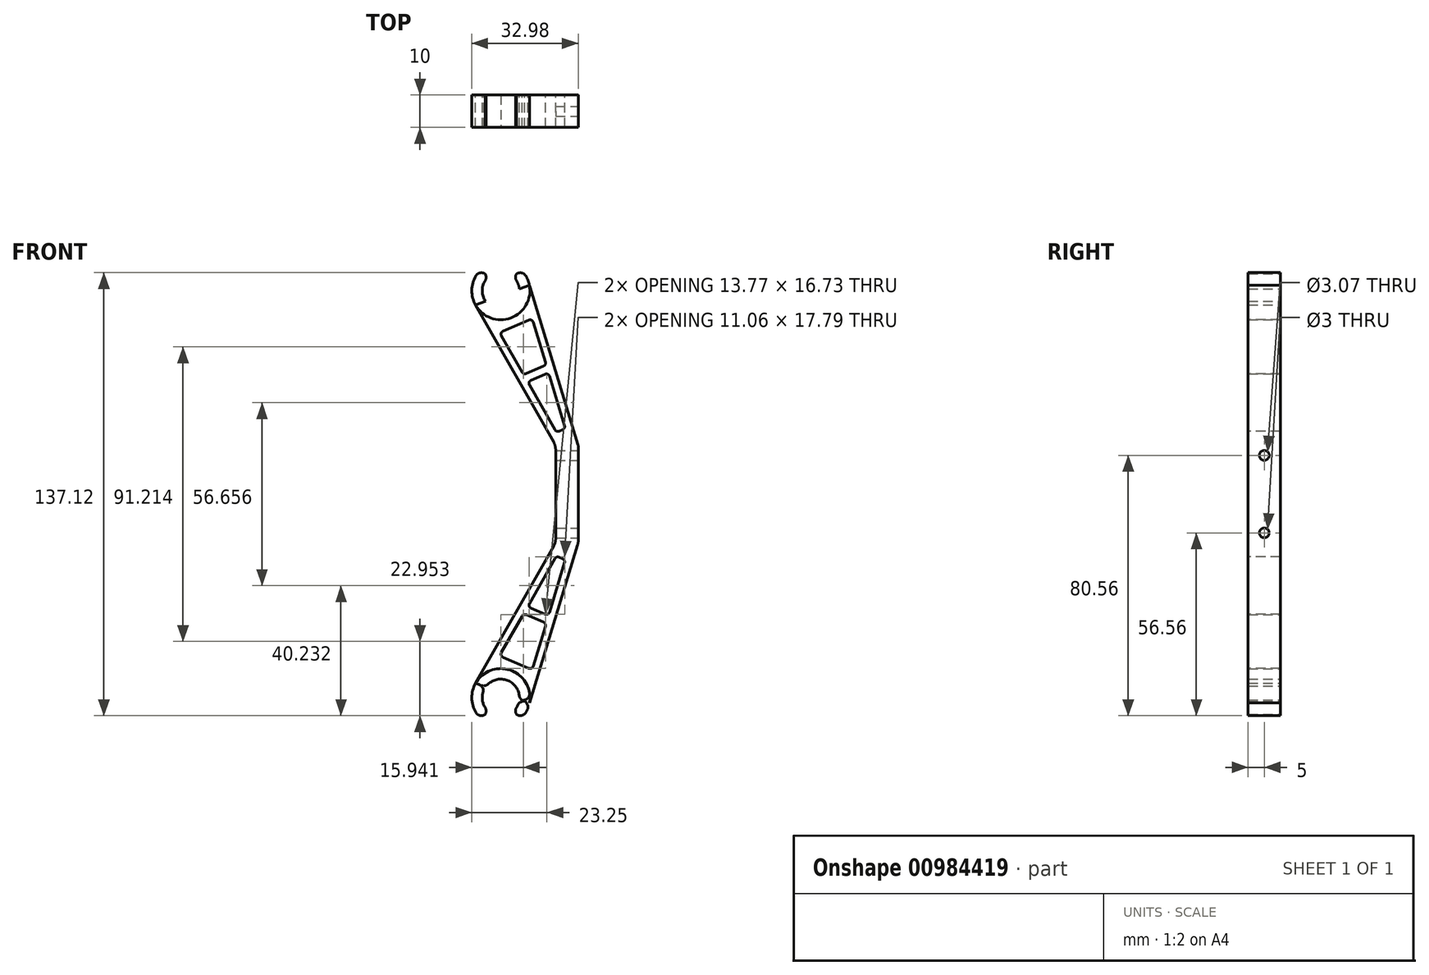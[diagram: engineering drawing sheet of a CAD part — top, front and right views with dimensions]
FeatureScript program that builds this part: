
annotation { "Feature Type Name" : "Feature", "Feature Type Description" : "" }
export const myFeature = defineFeature(function(context is Context, id is Id, definition is map)
    precondition{}
    {
        {
            var Q0;
            Q0=qCreatedBy(makeId("Front.planeOp"),FACE);
            var sketch = newSketch(context, id + "F0", { "sketchPlane" : qUnion([Q0])});
            skPoint(sketch, "E0.middle", {"position": v(16, 0) * mm});
            skCircle(sketch, "E1", {"center": v(-4.47, -63) * mm, "radius": 5.75 * mm});
            skCircle(sketch, "E2", {"center": v(-4.47, -63) * mm, "radius": 9 * mm});
            skLineSegment(sketch, "E3", {"start": v(12.5, -15) * mm, "end": v(-12.3, -58.55) * mm});
            skLineSegment(sketch, "E4", {"start": v(19.5, -15) * mm, "end": v(4.43, -64.65) * mm});
            skLineSegment(sketch, "E5", {"start": v(5.21, -54.33) * mm, "end": v(9.57, -39.98) * mm});
            skLineSegment(sketch, "E6", {"start": v(2.58, -36.97) * mm, "end": v(-4.84, -50) * mm});
            skLineSegment(sketch, "E7", {"start": v(-4.84, -50) * mm, "end": v(5.21, -54.33) * mm});
            skLineSegment(sketch, "E8", {"start": v(2.58, -36.97) * mm, "end": v(9.57, -39.98) * mm});
            skLineSegment(sketch, "E9", {"start": v(3.82, -34.8) * mm, "end": v(12.73, -19.16) * mm});
            skLineSegment(sketch, "E10", {"start": v(10.3, -37.59) * mm, "end": v(15.53, -20.36) * mm});
            skLineSegment(sketch, "E11", {"start": v(3.82, -34.8) * mm, "end": v(10.3, -37.59) * mm});
            skLineSegment(sketch, "E12", {"start": v(12.73, -19.16) * mm, "end": v(15.53, -20.36) * mm});
            skLineSegment(sketch, "E13.MirrorCS", {"start": v(12.73, 19.16) * mm, "end": v(15.53, 20.36) * mm});
            skLineSegment(sketch, "E14.MirrorCS", {"start": v(-4.84, 50) * mm, "end": v(5.21, 54.33) * mm});
            skLineSegment(sketch, "E15.MirrorCS", {"start": v(12.5, 15) * mm, "end": v(-12.3, 58.55) * mm});
            skLineSegment(sketch, "E16.MirrorCS", {"start": v(10.3, 37.59) * mm, "end": v(15.53, 20.36) * mm});
            skLineSegment(sketch, "E17.MirrorCS", {"start": v(3.82, 34.8) * mm, "end": v(12.73, 19.16) * mm});
            skLineSegment(sketch, "E18.MirrorCS", {"start": v(2.58, 36.97) * mm, "end": v(-4.84, 50) * mm});
            skLineSegment(sketch, "E19.MirrorCS", {"start": v(3.82, 34.8) * mm, "end": v(10.3, 37.59) * mm});
            skLineSegment(sketch, "E20.MirrorCS", {"start": v(19.5, 15) * mm, "end": v(4.43, 64.65) * mm});
            skLineSegment(sketch, "E21.MirrorCS", {"start": v(5.21, 54.33) * mm, "end": v(9.57, 39.98) * mm});
            skLineSegment(sketch, "E22.MirrorCS", {"start": v(2.58, 36.97) * mm, "end": v(9.57, 39.98) * mm});
            skLineSegment(sketch, "E23", {"start": v(12.5, -15) * mm, "end": v(12.5, 15) * mm});
            skLineSegment(sketch, "E24", {"start": v(19.5, 15) * mm, "end": v(19.5, -15) * mm});
            skLineSegment(sketch, "E25", {"start": v(-12.3, 58.55) * mm, "end": v(4.43, 64.65) * mm});
            skLineSegment(sketch, "E26", {"start": v(-12.3, -58.55) * mm, "end": v(4.43, -64.65) * mm});
            skLineSegment(sketch, "E27", {"start": v(-10.6, -69.6) * mm, "end": v(-8.38, -67.22) * mm});
            skLineSegment(sketch, "E28", {"start": v(1.65, -69.6) * mm, "end": v(-0.56, -67.22) * mm});
            skCircle(sketch, "E29.MirrorC", {"center": v(-4.47, 63) * mm, "radius": 9 * mm});
            skLineSegment(sketch, "E30.MirrorCS", {"start": v(1.65, 69.6) * mm, "end": v(-0.56, 67.22) * mm});
            skLineSegment(sketch, "E31.MirrorCS", {"start": v(-10.6, 69.6) * mm, "end": v(-8.38, 67.22) * mm});
            skCircle(sketch, "E32.MirrorC", {"center": v(-4.47, 63) * mm, "radius": 5.75 * mm});
            skSolve(sketch);
        }
        {
            var Q0;
            {var subQ6=sQuery(id+"F0.wireOp",EDGE,"E3");Q0=makeQuery(id+"F0.imprint","IMPRINT",FACE,{"disambiguationData":[TD([[makeQuery(id+"F0.imprint","IMPRINT",EDGE,{"derivedFrom":subQ6}),1.0]])]});}
            var Q1;
            {var subQ0=sQuery(id+"F0.wireOp",EDGE,"E26");var subQ1=sQuery(id+"F0.wireOp",EDGE,"E1");var subQ2=makeQuery(id+"F0.imprint","INTERSECT",VERTEX,{"disambiguationData":[OD(0.0)],"derivedFrom":[subQ1,subQ0]});Q1=makeQuery(id+"F0.imprint","IMPRINT",FACE,{"disambiguationData":[TD([[makeQuery(id+"F0.imprint","IMPRINT",EDGE,{"disambiguationData":[TD([[subQ2,1.0]])],"derivedFrom":subQ1}),-1.0]])]});}
            var Q2;
            {var subQ0=sQuery(id+"F0.wireOp",EDGE,"XQdszwVE-5wpe-kycQ-sRSQ-Fq0FjsTCC5aD");Q2=makeQuery(id+"F0.imprint","IMPRINT",FACE,{"disambiguationData":[TD([[makeQuery(id+"F0.imprint","IMPRINT",EDGE,{"derivedFrom":subQ0}),1.0]])]});}
            var Q3;
            {var subQ0=sQuery(id+"F0.wireOp",EDGE,"Yc0Pc47L-QJd6-gHrf-0qyo-1opZ7JtCYNZG");Q3=makeQuery(id+"F0.imprint","IMPRINT",FACE,{"disambiguationData":[TD([[makeQuery(id+"F0.imprint","IMPRINT",EDGE,{"derivedFrom":subQ0}),-1.0]])]});}
            var Q4;
            {var subQ0=sQuery(id+"F0.wireOp",EDGE,"E25");var subQ4=sQuery(id+"F0.wireOp",EDGE,"E143.MirrorC");var subQ5=makeQuery(id+"F0.imprint","INTERSECT",VERTEX,{"disambiguationData":[OD(0.0)],"derivedFrom":[subQ4,subQ0]});Q4=makeQuery(id+"F0.imprint","IMPRINT",FACE,{"disambiguationData":[TD([[makeQuery(id+"F0.imprint","IMPRINT",EDGE,{"disambiguationData":[TD([[subQ5,1.0]])],"derivedFrom":subQ4}),1.0]])]});}
            var Q5;
            {var subQ0=sQuery(id+"F0.wireOp",EDGE,"b6da1f22-f3a6-460e-9121-5a5fd05a2c0d7.MirrorCS");Q5=makeQuery(id+"F0.imprint","IMPRINT",FACE,{"disambiguationData":[TD([[makeQuery(id+"F0.imprint","IMPRINT",EDGE,{"derivedFrom":subQ0}),1.0]])]});}
            var Q6;
            {var subQ3=sQuery(id+"F0.wireOp",EDGE,"E141.MirrorCS");Q6=makeQuery(id+"F0.imprint","IMPRINT",FACE,{"disambiguationData":[TD([[makeQuery(id+"F0.imprint","IMPRINT",EDGE,{"derivedFrom":subQ3}),-1.0]])]});}
            var Q7;
            {var subQ0=sQuery(id+"F0.wireOp",EDGE,"E27");Q7=makeQuery(id+"F0.imprint","IMPRINT",FACE,{"disambiguationData":[TD([[makeQuery(id+"F0.imprint","IMPRINT",EDGE,{"derivedFrom":subQ0}),1.0]])]});}
            var Q8;
            {var subQ0=sQuery(id+"F0.wireOp",EDGE,"E28");Q8=makeQuery(id+"F0.imprint","IMPRINT",FACE,{"disambiguationData":[TD([[makeQuery(id+"F0.imprint","IMPRINT",EDGE,{"derivedFrom":subQ0}),-1.0]])]});}
            var Q9;
            {var subQ0=sQuery(id+"F0.wireOp",EDGE,"E25");var subQ1=sQuery(id+"F0.wireOp",EDGE,"E29.MirrorC");var subQ3=makeQuery(id+"F0.imprint","INTERSECT",VERTEX,{"derivedFrom":[subQ1,subQ0]});Q9=makeQuery(id+"F0.imprint","IMPRINT",FACE,{"disambiguationData":[TD([[makeQuery(id+"F0.imprint","IMPRINT",EDGE,{"disambiguationData":[TD([[subQ3,1.0]])],"derivedFrom":subQ0}),-1.0]])]});}
            var Q10;
            {var subQ3=sQuery(id+"F0.wireOp",EDGE,"E31.MirrorCS");Q10=makeQuery(id+"F0.imprint","IMPRINT",FACE,{"disambiguationData":[TD([[makeQuery(id+"F0.imprint","IMPRINT",EDGE,{"derivedFrom":subQ3}),-1.0]])]});}
            var Q11;
            {var subQ0=sQuery(id+"F0.wireOp",EDGE,"E30.MirrorCS");Q11=makeQuery(id+"F0.imprint","IMPRINT",FACE,{"disambiguationData":[TD([[makeQuery(id+"F0.imprint","IMPRINT",EDGE,{"derivedFrom":subQ0}),1.0]])]});}
            extrude(context, id + "F1", {"entities" : qUnion([Q0, Q1, Q2, Q3, Q4, Q5, Q6, Q7, Q8, Q9, Q10, Q11]), "depth" : 10 * mm, "offsetDistance" : 25 * mm});
        }
        {
            var Q0;
            Q0=makeQuery(id+"F1.opExtrude","SWEPT_EDGE",EDGE,{"disambiguationData":[OSD([sQuery(id+"F0.wireOp",EDGE,"E10"),sQuery(id+"F0.wireOp",EDGE,"E12")])]});
            var Q1;
            Q1=makeQuery(id+"F1.opExtrude","SWEPT_EDGE",EDGE,{"disambiguationData":[OSD([sQuery(id+"F0.wireOp",EDGE,"E9"),sQuery(id+"F0.wireOp",EDGE,"E12")])]});
            var Q2;
            Q2=makeQuery(id+"F1.opExtrude","SWEPT_EDGE",EDGE,{"disambiguationData":[OSD([sQuery(id+"F0.wireOp",EDGE,"E9"),sQuery(id+"F0.wireOp",EDGE,"E11")])]});
            var Q3;
            Q3=makeQuery(id+"F1.opExtrude","SWEPT_EDGE",EDGE,{"disambiguationData":[OSD([sQuery(id+"F0.wireOp",EDGE,"E10"),sQuery(id+"F0.wireOp",EDGE,"E11")])]});
            var Q4;
            Q4=makeQuery(id+"F1.opExtrude","SWEPT_EDGE",EDGE,{"disambiguationData":[OSD([sQuery(id+"F0.wireOp",EDGE,"E5"),sQuery(id+"F0.wireOp",EDGE,"E8")])]});
            var Q5;
            Q5=makeQuery(id+"F1.opExtrude","SWEPT_EDGE",EDGE,{"disambiguationData":[OSD([sQuery(id+"F0.wireOp",EDGE,"E6"),sQuery(id+"F0.wireOp",EDGE,"E8")])]});
            var Q6;
            Q6=makeQuery(id+"F1.opExtrude","SWEPT_EDGE",EDGE,{"disambiguationData":[OSD([sQuery(id+"F0.wireOp",EDGE,"E5"),sQuery(id+"F0.wireOp",EDGE,"E7")])]});
            var Q7;
            Q7=makeQuery(id+"F1.opExtrude","SWEPT_EDGE",EDGE,{"disambiguationData":[OSD([sQuery(id+"F0.wireOp",EDGE,"E6"),sQuery(id+"F0.wireOp",EDGE,"E7")])]});
            var Q8;
            Q8=makeQuery(id+"F1.opExtrude","SWEPT_EDGE",EDGE,{"disambiguationData":[OSD([sQuery(id+"F0.wireOp",EDGE,"E13.MirrorCS"),sQuery(id+"F0.wireOp",EDGE,"E16.MirrorCS")])]});
            var Q9;
            Q9=makeQuery(id+"F1.opExtrude","SWEPT_EDGE",EDGE,{"disambiguationData":[OSD([sQuery(id+"F0.wireOp",EDGE,"E13.MirrorCS"),sQuery(id+"F0.wireOp",EDGE,"E17.MirrorCS")])]});
            var Q10;
            Q10=makeQuery(id+"F1.opExtrude","SWEPT_EDGE",EDGE,{"disambiguationData":[OSD([sQuery(id+"F0.wireOp",EDGE,"E17.MirrorCS"),sQuery(id+"F0.wireOp",EDGE,"E19.MirrorCS")])]});
            var Q11;
            Q11=makeQuery(id+"F1.opExtrude","SWEPT_EDGE",EDGE,{"disambiguationData":[OSD([sQuery(id+"F0.wireOp",EDGE,"E16.MirrorCS"),sQuery(id+"F0.wireOp",EDGE,"E19.MirrorCS")])]});
            var Q12;
            Q12=makeQuery(id+"F1.opExtrude","SWEPT_EDGE",EDGE,{"disambiguationData":[OSD([sQuery(id+"F0.wireOp",EDGE,"E14.MirrorCS"),sQuery(id+"F0.wireOp",EDGE,"E21.MirrorCS")])]});
            var Q13;
            Q13=makeQuery(id+"F1.opExtrude","SWEPT_EDGE",EDGE,{"disambiguationData":[OSD([sQuery(id+"F0.wireOp",EDGE,"E14.MirrorCS"),sQuery(id+"F0.wireOp",EDGE,"E18.MirrorCS")])]});
            var Q14;
            Q14=makeQuery(id+"F1.opExtrude","SWEPT_EDGE",EDGE,{"disambiguationData":[OSD([sQuery(id+"F0.wireOp",EDGE,"E18.MirrorCS"),sQuery(id+"F0.wireOp",EDGE,"E22.MirrorCS")])]});
            var Q15;
            Q15=makeQuery(id+"F1.opExtrude","SWEPT_EDGE",EDGE,{"disambiguationData":[OSD([sQuery(id+"F0.wireOp",EDGE,"E21.MirrorCS"),sQuery(id+"F0.wireOp",EDGE,"E22.MirrorCS")])]});
            fillet(context, id + "F2", {"entities" : qUnion([Q0, Q1, Q2, Q3, Q4, Q5, Q6, Q7, Q8, Q9, Q10, Q11, Q12, Q13, Q14, Q15]), "radius" : 1 * mm, "tangentPropagation" : true, "allowEdgeOverflow" : false});
        }
        {
            var Q0;
            Q0=makeQuery(id+"F1.opExtrude","SWEPT_EDGE",EDGE,{"disambiguationData":[OSD([sQuery(id+"F0.wireOp",EDGE,"b6da1f22-f3a6-460e-9121-5a5fd05a2c0d4.MirrorC"),sQuery(id+"F0.wireOp",EDGE,"E141.MirrorCS")])]});
            var Q1;
            Q1=makeQuery(id+"F1.opExtrude","SWEPT_EDGE",EDGE,{"disambiguationData":[OSD([sQuery(id+"F0.wireOp",EDGE,"E141.MirrorCS"),sQuery(id+"F0.wireOp",EDGE,"E143.MirrorC")])]});
            var Q2;
            Q2=makeQuery(id+"F1.opExtrude","SWEPT_EDGE",EDGE,{"disambiguationData":[OSD([sQuery(id+"F0.wireOp",EDGE,"b6da1f22-f3a6-460e-9121-5a5fd05a2c0d7.MirrorCS"),sQuery(id+"F0.wireOp",EDGE,"E143.MirrorC")])]});
            var Q3;
            Q3=makeQuery(id+"F1.opExtrude","SWEPT_EDGE",EDGE,{"disambiguationData":[OSD([sQuery(id+"F0.wireOp",EDGE,"b6da1f22-f3a6-460e-9121-5a5fd05a2c0d4.MirrorC"),sQuery(id+"F0.wireOp",EDGE,"b6da1f22-f3a6-460e-9121-5a5fd05a2c0d7.MirrorCS")])]});
            var Q4;
            Q4=makeQuery(id+"F1.opExtrude","SWEPT_EDGE",EDGE,{"disambiguationData":[OSD([sQuery(id+"F0.wireOp",EDGE,"E2"),sQuery(id+"F0.wireOp",EDGE,"Yc0Pc47L-QJd6-gHrf-0qyo-1opZ7JtCYNZG")])]});
            var Q5;
            Q5=makeQuery(id+"F1.opExtrude","SWEPT_EDGE",EDGE,{"disambiguationData":[OSD([sQuery(id+"F0.wireOp",EDGE,"E1"),sQuery(id+"F0.wireOp",EDGE,"Yc0Pc47L-QJd6-gHrf-0qyo-1opZ7JtCYNZG")])]});
            var Q6;
            Q6=makeQuery(id+"F1.opExtrude","SWEPT_EDGE",EDGE,{"disambiguationData":[OSD([sQuery(id+"F0.wireOp",EDGE,"E1"),sQuery(id+"F0.wireOp",EDGE,"XQdszwVE-5wpe-kycQ-sRSQ-Fq0FjsTCC5aD")])]});
            var Q7;
            Q7=makeQuery(id+"F1.opExtrude","SWEPT_EDGE",EDGE,{"disambiguationData":[OSD([sQuery(id+"F0.wireOp",EDGE,"E2"),sQuery(id+"F0.wireOp",EDGE,"XQdszwVE-5wpe-kycQ-sRSQ-Fq0FjsTCC5aD")])]});
            var Q8;
            Q8=makeQuery(id+"F1.opExtrude","SWEPT_EDGE",EDGE,{"disambiguationData":[OSD([sQuery(id+"F0.wireOp",EDGE,"E20.MirrorCS"),sQuery(id+"F0.wireOp",EDGE,"E25")])]});
            var Q9;
            Q9=makeQuery(id+"F1.opExtrude","SWEPT_EDGE",EDGE,{"disambiguationData":[OSD([sQuery(id+"F0.wireOp",EDGE,"E29.MirrorC"),sQuery(id+"F0.wireOp",EDGE,"E30.MirrorCS")])]});
            var Q10;
            Q10=makeQuery(id+"F1.opExtrude","SWEPT_EDGE",EDGE,{"disambiguationData":[OSD([sQuery(id+"F0.wireOp",EDGE,"E30.MirrorCS"),sQuery(id+"F0.wireOp",EDGE,"E32.MirrorC")])]});
            var Q11;
            Q11=makeQuery(id+"F1.opExtrude","SWEPT_EDGE",EDGE,{"disambiguationData":[OSD([sQuery(id+"F0.wireOp",EDGE,"E31.MirrorCS"),sQuery(id+"F0.wireOp",EDGE,"E32.MirrorC")])]});
            var Q12;
            Q12=makeQuery(id+"F1.opExtrude","SWEPT_EDGE",EDGE,{"disambiguationData":[OSD([sQuery(id+"F0.wireOp",EDGE,"E29.MirrorC"),sQuery(id+"F0.wireOp",EDGE,"E31.MirrorCS")])]});
            fillet(context, id + "F3", {"entities" : qUnion([Q0, Q1, Q2, Q3, Q4, Q5, Q6, Q7, Q8, Q9, Q10, Q11, Q12]), "radius" : 2 * mm, "tangentPropagation" : true, "allowEdgeOverflow" : false});
        }
        {
            var Q0;
            Q0=makeQuery(id+"F1.opExtrude","SWEPT_EDGE",EDGE,{"disambiguationData":[OSD([sQuery(id+"F0.wireOp",EDGE,"E3"),sQuery(id+"F0.wireOp",EDGE,"E23")])]});
            var Q1;
            Q1=makeQuery(id+"F1.opExtrude","SWEPT_EDGE",EDGE,{"disambiguationData":[OSD([sQuery(id+"F0.wireOp",EDGE,"E15.MirrorCS"),sQuery(id+"F0.wireOp",EDGE,"E23")])]});
            var Q2;
            Q2=makeQuery(id+"F1.opExtrude","SWEPT_EDGE",EDGE,{"disambiguationData":[OSD([sQuery(id+"F0.wireOp",EDGE,"E4"),sQuery(id+"F0.wireOp",EDGE,"E24")])]});
            var Q3;
            Q3=makeQuery(id+"F1.opExtrude","SWEPT_EDGE",EDGE,{"disambiguationData":[OSD([sQuery(id+"F0.wireOp",EDGE,"E20.MirrorCS"),sQuery(id+"F0.wireOp",EDGE,"E24")])]});
            fillet(context, id + "F4", {"entities" : qUnion([Q0, Q1, Q2, Q3]), "radius" : 5 * mm, "tangentPropagation" : true, "allowEdgeOverflow" : false});
        }
        {
            var Q0;
            Q0=makeQuery(id+"F1.opExtrude","SWEPT_FACE",FACE,{"disambiguationData":[OSD([sQuery(id+"F0.wireOp",EDGE,"E24")])]});
            var sketch = newSketch(context, id + "F5", { "sketchPlane" : qUnion([Q0])});
            skCircle(sketch, "E33", {"center": v(-5, -12) * mm, "radius": 1.5 * mm});
            skCircle(sketch, "E34", {"center": v(-5, 12) * mm, "radius": 1.53 * mm});
            skSolve(sketch);
        }
        {
            var Q0;
            Q0=makeQuery(id+"F5.imprint","IMPRINT",FACE,{"disambiguationData":[TD([[makeQuery(id+"F5.imprint","IMPRINT",EDGE,{"derivedFrom":sQuery(id+"F5.wireOp",EDGE,"E33")}),1.0]])]});
            var Q1;
            Q1=makeQuery(id+"F5.imprint","IMPRINT",FACE,{"disambiguationData":[TD([[makeQuery(id+"F5.imprint","IMPRINT",EDGE,{"derivedFrom":sQuery(id+"F5.wireOp",EDGE,"E34")}),1.0]])]});
            extrude(context, id + "F6", {"entities" : qUnion([Q0, Q1]), "operationType" : NewBodyOperationType.REMOVE, "oppositeDirection" : true, "depth" : 25 * mm, "offsetDistance" : 25 * mm});
        }
    });
